# Revit family: 94861220
name_source: partatom
category: Modelos genéricos
revit_build: Autodesk Revit 2016 (Build: 20150220_1215(x64)
units: mm (PartAtom-declared; Revit-internal decimal feet)

## family parameters
Com base no plano de trabalho = Não
Compartilhado = Não
Corte com vazios quando carregados = Não
Cota do conector redondo = Utilizar diâmetro
Pode hospedar o vergalhão = Não
Ponto de cálculo do ambiente = Não
Sempre na vertical = Sim
Tipo de parte = Normal

## types (1)
- Tramontina TDC Forno - 94861/220
    Capacidade = 69 L
    Comentários de tipos = Ler Manual de Instalação
    Código de montagem = 94861/220
    Descrição = Tramontina TDC - Ready Cook 60 - 94861/220
    Desenvolvedor = Factory Cursos & Desenvolvimento
    Fabricante = Tramontina
    Frequencia = 60  [stored 0.19685 ft]
    Nicho de Instalação = 350X481X409
    Niveis de Temp. = 9
    Potencia Máxima = 2900 W
    Referencia = 94861/220
    Site do desenvolvedor = www.factorycursos.com.br
    Tensão = 220  [stored 0.721785 ft]
    Tipo de imagem = <Nenhum>
    URL = www.tramontina.com.br

note: [stored X ft] marks values corroborated as IEEE doubles in the binary element streams (Revit-internal decimal feet)
